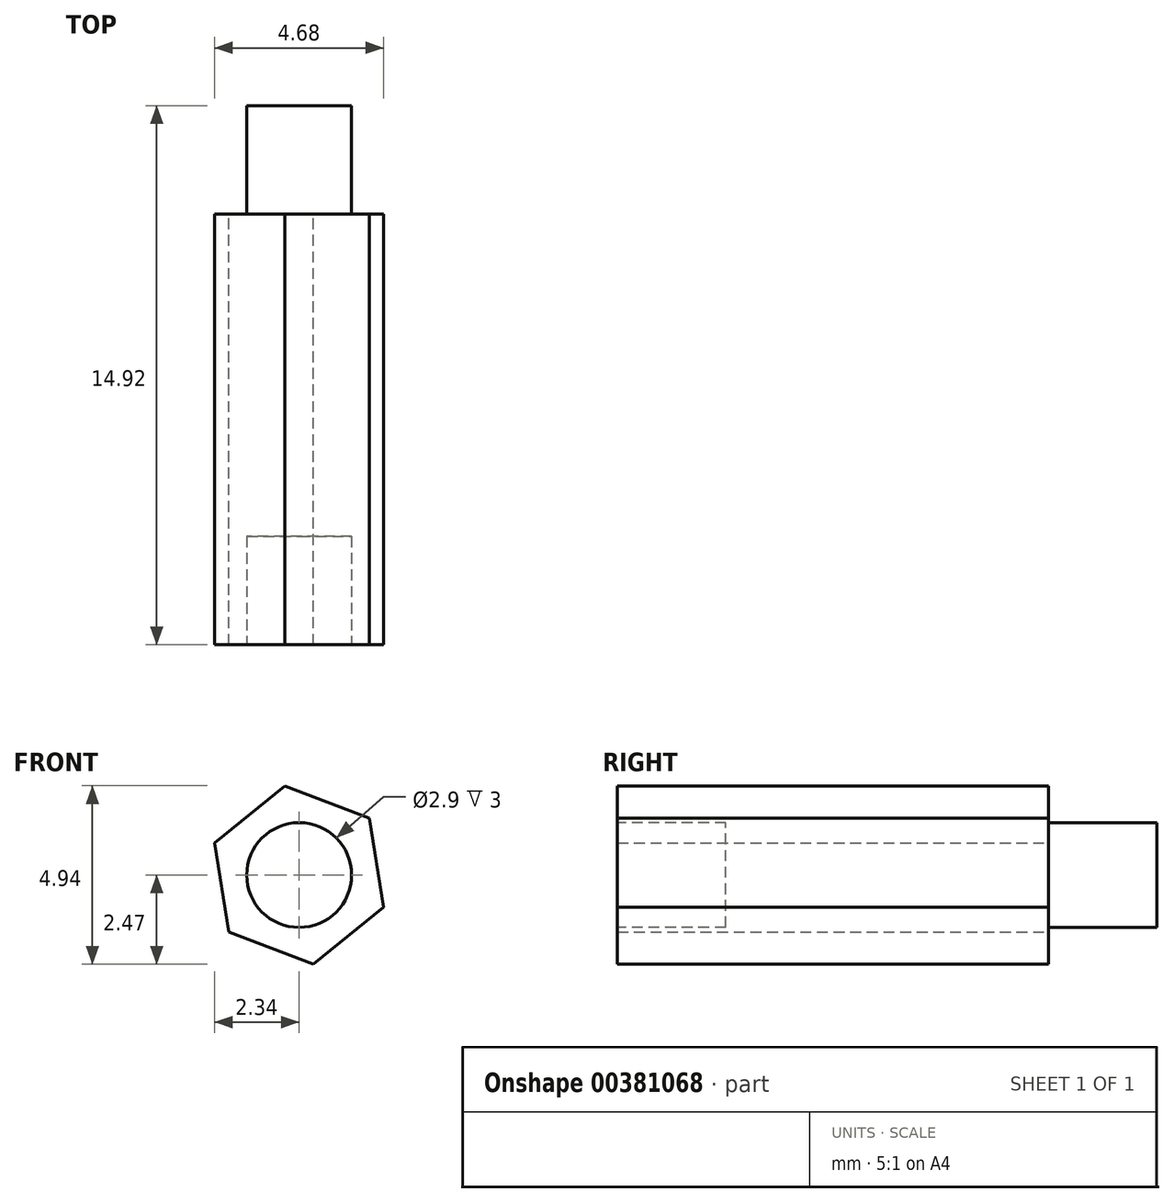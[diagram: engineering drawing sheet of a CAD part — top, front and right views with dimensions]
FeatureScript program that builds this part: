
annotation { "Feature Type Name" : "Feature", "Feature Type Description" : "" }
export const myFeature = defineFeature(function(context is Context, id is Id, definition is map)
    precondition{}
    {
        {
            var Q0;
            Q0=qCreatedBy(makeId("Front.planeOp"),FACE);
            var sketch = newSketch(context, id + "F0", { "sketchPlane" : qUnion([Q0])});
            skCircle(sketch, "E0.cCircle", {"center": v(0, 0) * mm, "radius": 2.5 * mm, "construction": true});
            skLineSegment(sketch, "E0.0", {"start": v(1.94, 1.58) * mm, "end": v(2.34, -0.9) * mm});
            skLineSegment(sketch, "E0.1", {"start": v(2.34, -0.9) * mm, "end": v(0.4, -2.47) * mm});
            skLineSegment(sketch, "E0.2", {"start": v(0.4, -2.47) * mm, "end": v(-1.94, -1.58) * mm});
            skLineSegment(sketch, "E0.3", {"start": v(-1.94, -1.58) * mm, "end": v(-2.34, 0.9) * mm});
            skLineSegment(sketch, "E0.4", {"start": v(-2.34, 0.9) * mm, "end": v(-0.4, 2.47) * mm});
            skLineSegment(sketch, "E0.5", {"start": v(-0.4, 2.47) * mm, "end": v(1.94, 1.58) * mm});
            skSolve(sketch);
        }
        {
            var Q0;
            Q0 = qSketchRegion(id + "F0", true);
            extrude(context, id + "F1", {"entities" : qUnion([Q0]), "depth" : 11.92 * mm});
        }
        {
            var Q0;
            Q0=makeQuery(id+"F1.opExtrude","CAP_FACE",FACE,{"disambiguationData":[OSD([sQuery(id+"F0.wireOp",EDGE,"E0.0"),sQuery(id+"F0.wireOp",EDGE,"E0.1"),sQuery(id+"F0.wireOp",EDGE,"E0.2"),sQuery(id+"F0.wireOp",EDGE,"E0.3"),sQuery(id+"F0.wireOp",EDGE,"E0.4"),sQuery(id+"F0.wireOp",EDGE,"E0.5")])],"isStart":true});
            var sketch = newSketch(context, id + "F2", { "sketchPlane" : qUnion([Q0])});
            skCircle(sketch, "E1", {"center": v(0, 0) * mm, "radius": 1.45 * mm});
            skSolve(sketch);
        }
        {
            var Q0;
            Q0=makeQuery(id+"F2.imprint","IMPRINT",FACE,{"disambiguationData":[TD([[makeQuery(id+"F2.imprint","IMPRINT",EDGE,{"derivedFrom":sQuery(id+"F2.wireOp",EDGE,"E1")}),1.0]])]});
            extrude(context, id + "F3", {"entities" : qUnion([Q0]), "operationType" : NewBodyOperationType.ADD, "depth" : 3 * mm});
        }
        {
            var Q0;
            Q0=makeQuery(id+"F1.opExtrude","CAP_FACE",FACE,{"disambiguationData":[OSD([sQuery(id+"F0.wireOp",EDGE,"E0.0"),sQuery(id+"F0.wireOp",EDGE,"E0.1"),sQuery(id+"F0.wireOp",EDGE,"E0.2"),sQuery(id+"F0.wireOp",EDGE,"E0.3"),sQuery(id+"F0.wireOp",EDGE,"E0.4"),sQuery(id+"F0.wireOp",EDGE,"E0.5")])],"isStart":false});
            var sketch = newSketch(context, id + "F4", { "sketchPlane" : qUnion([Q0])});
            skCircle(sketch, "E2", {"center": v(0, 0) * mm, "radius": 1.45 * mm});
            skSolve(sketch);
        }
        {
            var Q0;
            Q0 = qSketchRegion(id + "F4", true);
            extrude(context, id + "F5", {"entities" : qUnion([Q0]), "operationType" : NewBodyOperationType.REMOVE, "oppositeDirection" : true, "depth" : 3 * mm});
        }
    });
